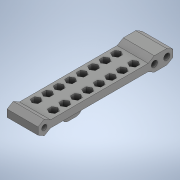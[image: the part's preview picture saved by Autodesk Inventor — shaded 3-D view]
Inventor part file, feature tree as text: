
AUTODESK INVENTOR PART (.ipt)
format: ipt  version: 2020 (Build 240168000, 168)  size: 477,184 bytes
history: native  units: in
note: dims shown in document units (in); Inventor stores cm internally (conversion verified against a paired STEP export)
features: sketch x7, extrude x6, projected_geometry x4, plane x2, mirror x1, fillet x1
ambient origin geometry x8: Origin, YZ Plane, XZ Plane, XY Plane, X Axis, Y Axis, Z Axis, Center Point
bodies: Solid1 (feature_tree)
feature tree (21):
  extrude  "Extrusion1"  Depth=3.4256in
  plane  "Work Plane1"
  extrude  "Extrusion2"  Depth=0.7874in
  sketch  "Sketch4"  dims[d4=0.0in d5=0.0827in]
  extrude  "Extrusion4"  Depth=0.0827in
  plane  "Work Plane2"
  extrude  "Extrusion6"  Depth=3.1106in
  mirror  "Mirror2"
  extrude  "Extrusion7"  Depth=0.315in
  extrude  "Extrusion8"  Depth=0.2362in
  fillet  "Fillet1"  [1 undecoded]
  sketch  "Sketch1"  dims[d0=0.1818in d1=3.4256in]
  sketch  "Sketch2"  dims[d2=0.1339in d3=0.7874in]
  sketch  "Sketch5"  dims[d6=0.7874in d7=0.0in d28=3.1106in]
  sketch  "Sketch7"  dims[d29=0.315in d31=0.315in]
  projected_geometry  "Projected Loop7"
  projected_geometry  "Projected Loop8"
  sketch  "Sketch8"  dims[d33=0.1575in d34=0.2362in d35=0.0in]
  projected_geometry  "Projected Loop9"
  sketch  "Sketch10"  dims[d38=0.315in d39=0.2756in d40=-0.3092in d41=0.0787in d42=0.0787in d43=0.0787in d44=3.1496in d46=0.2913in d47=0.3937in d49=0.3937in d51=3.1496in d53=0.2913in d54=0.3937in d56=0.3937in d58=0.0in d59=0.0in d60=1.0994in d61=0.1378in d63=1.1811in d64=0.1575in d65=0.0in d66=0.126in d67=0.1575in]
  projected_geometry  "Projected Loop10"
note: 1 required parameter value undecoded (feature->parameter linkage not recoverable at this tier; creation-order binding heuristic only, values carry confidence <= 0.55)
